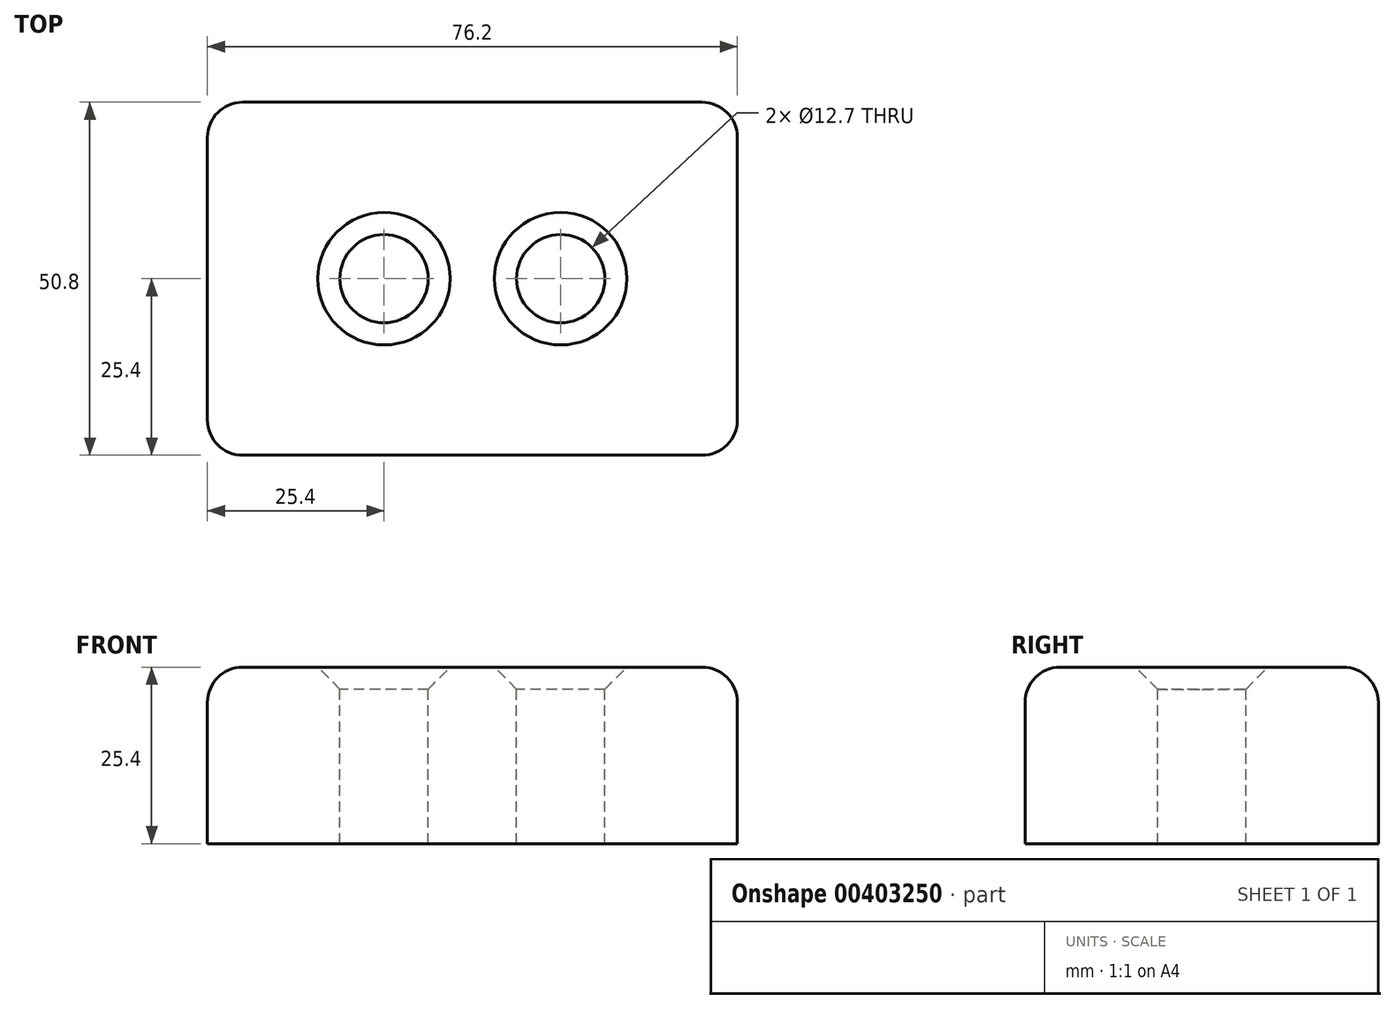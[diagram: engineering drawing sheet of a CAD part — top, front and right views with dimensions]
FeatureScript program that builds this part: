
annotation { "Feature Type Name" : "Feature", "Feature Type Description" : "" }
export const myFeature = defineFeature(function(context is Context, id is Id, definition is map)
    precondition{}
    {
        {
            var Q0;
            Q0=qCreatedBy(makeId("Top.planeOp"),FACE);
            var sketch = newSketch(context, id + "F0", { "sketchPlane" : qUnion([Q0])});
            skLineSegment(sketch, "E0.bottom", {"start": v(38.1, -25.4) * mm, "end": v(-38.1, -25.4) * mm});
            skLineSegment(sketch, "E0.top", {"start": v(38.1, 25.4) * mm, "end": v(-38.1, 25.4) * mm});
            skLineSegment(sketch, "E0.left", {"start": v(38.1, -25.4) * mm, "end": v(38.1, 25.4) * mm});
            skLineSegment(sketch, "E0.right", {"start": v(-38.1, -25.4) * mm, "end": v(-38.1, 25.4) * mm});
            skPoint(sketch, "E0.middle", {"position": v(0, 0) * mm});
            skSolve(sketch);
        }
        {
            var Q0;
            Q0=makeQuery(id+"F0.imprint","IMPRINT",FACE,{"disambiguationData":[TD([[makeQuery(id+"F0.imprint","IMPRINT",EDGE,{"derivedFrom":sQuery(id+"F0.wireOp",EDGE,"E0.bottom")}),-1.0]])]});
            extrude(context, id + "F1", {"entities" : qUnion([Q0]), "depth" : 25.4 * mm});
        }
        {
            var Q0;
            Q0=makeQuery(id+"F1.opExtrude","CAP_FACE",FACE,{"disambiguationData":[OSD([sQuery(id+"F0.wireOp",EDGE,"E0.bottom"),sQuery(id+"F0.wireOp",EDGE,"E0.top"),sQuery(id+"F0.wireOp",EDGE,"E0.left"),sQuery(id+"F0.wireOp",EDGE,"E0.right")])],"isStart":false});
            var Q1;
            Q1=makeQuery(id+"F1.opExtrude","SWEPT_EDGE",EDGE,{"disambiguationData":[OSD([sQuery(id+"F0.wireOp",EDGE,"E0.bottom"),sQuery(id+"F0.wireOp",EDGE,"E0.left")])]});
            var Q2;
            Q2=makeQuery(id+"F1.opExtrude","SWEPT_EDGE",EDGE,{"disambiguationData":[OSD([sQuery(id+"F0.wireOp",EDGE,"E0.top"),sQuery(id+"F0.wireOp",EDGE,"E0.left")])]});
            var Q3;
            Q3=makeQuery(id+"F1.opExtrude","SWEPT_EDGE",EDGE,{"disambiguationData":[OSD([sQuery(id+"F0.wireOp",EDGE,"E0.top"),sQuery(id+"F0.wireOp",EDGE,"E0.right")])]});
            var Q4;
            Q4=makeQuery(id+"F1.opExtrude","SWEPT_EDGE",EDGE,{"disambiguationData":[OSD([sQuery(id+"F0.wireOp",EDGE,"E0.bottom"),sQuery(id+"F0.wireOp",EDGE,"E0.right")])]});
            fillet(context, id + "F2", {"entities" : qUnion([Q0, Q1, Q2, Q3, Q4]), "radius" : 5.08 * mm, "tangentPropagation" : true, "allowEdgeOverflow" : false});
        }
        {
            var Q0;
            Q0=makeQuery(id+"F1.opExtrude","CAP_FACE",FACE,{"disambiguationData":[OSD([sQuery(id+"F0.wireOp",EDGE,"E0.bottom"),sQuery(id+"F0.wireOp",EDGE,"E0.top"),sQuery(id+"F0.wireOp",EDGE,"E0.left"),sQuery(id+"F0.wireOp",EDGE,"E0.right")])],"isStart":false});
            var sketch = newSketch(context, id + "F3", { "sketchPlane" : qUnion([Q0])});
            skLineSegment(sketch, "E1", {"start": v(-38.1, 0) * mm, "end": v(38.1, 0) * mm, "construction": true});
            skLineSegment(sketch, "E2", {"start": v(-12.7, 25.4) * mm, "end": v(-12.7, -25.4) * mm, "construction": true});
            skLineSegment(sketch, "E3", {"start": v(12.7, 25.4) * mm, "end": v(12.7, -25.4) * mm, "construction": true});
            skPoint(sketch, "E4", {"position": v(-12.7, 0) * mm});
            skPoint(sketch, "E5", {"position": v(12.7, 0) * mm});
            skSolve(sketch);
        }
        {
            var Q0;
            Q0=sQuery(id+"F3.wireOp",VERTEX,"E4");
            var Q1;
            Q1=sQuery(id+"F3.wireOp",VERTEX,"E5");
            var Q2;
            Q2=makeQuery(id+"F1.opExtrude","SWEPT_BODY",BODY,{"disambiguationData":[OSD([sQuery(id+"F0.wireOp",EDGE,"E0.bottom"),sQuery(id+"F0.wireOp",EDGE,"E0.top"),sQuery(id+"F0.wireOp",EDGE,"E0.left"),sQuery(id+"F0.wireOp",EDGE,"E0.right")])]});
            hole(context, id + "F4", {"style" : HoleStyle.C_SINK, "endStyle" : HoleEndStyle.THROUGH, "holeDiameter" : 12.7 * mm, "cSinkDiameter" : 19.05 * mm, "cSinkAngle" : 90 * degree, "isTappedThrough" : true, "tappedDepth" : 12.7 * mm, "tapClearance" : 3, "locations" : qUnion([Q0, Q1]), "scope" : qUnion([Q2])});
        }
    });
